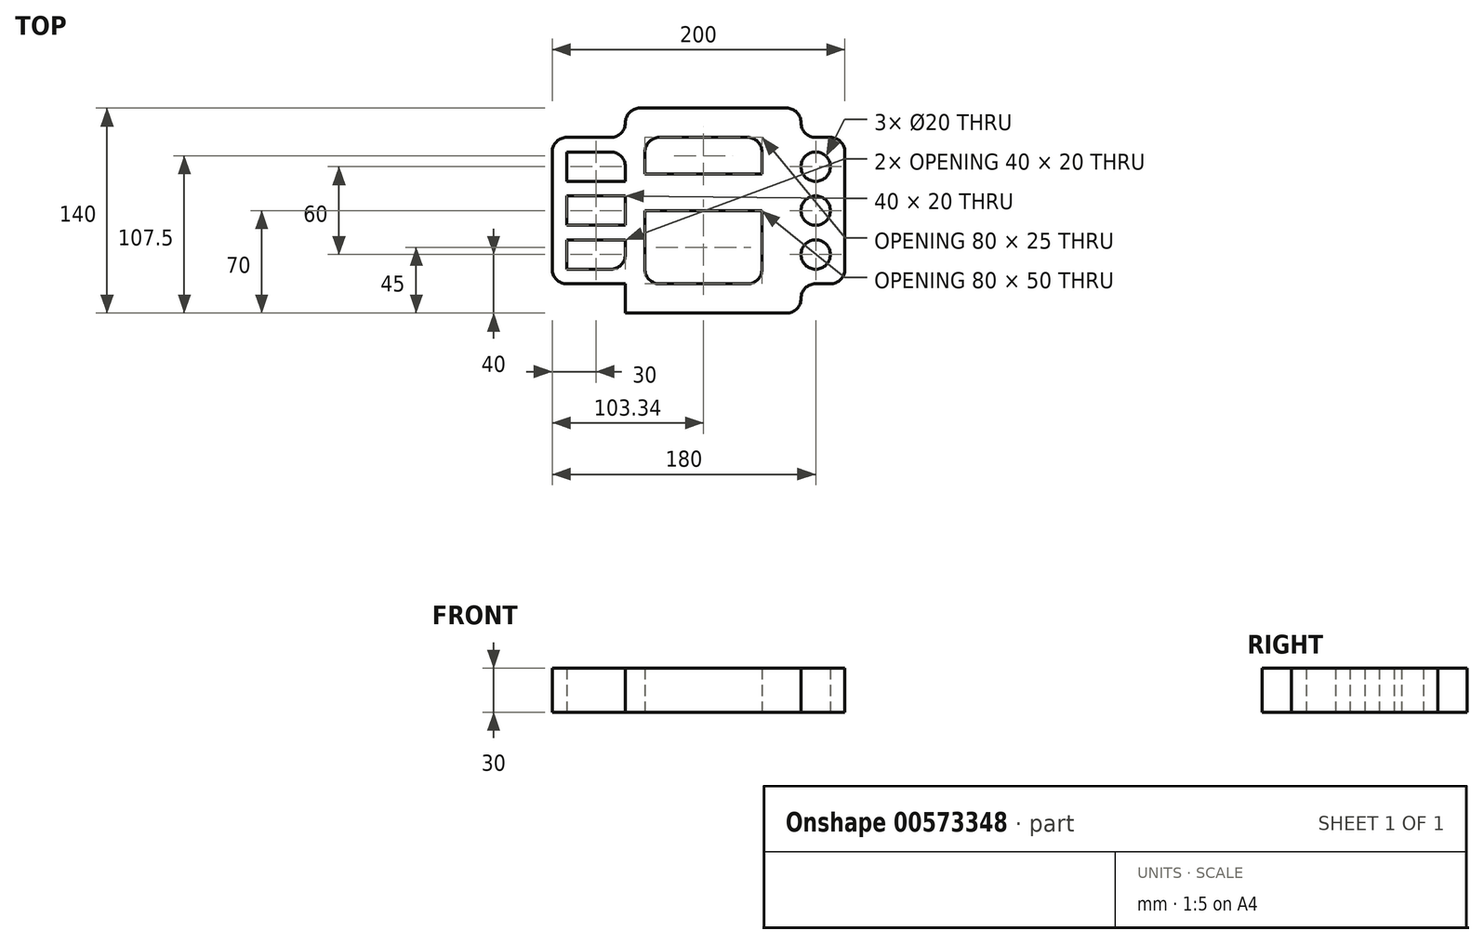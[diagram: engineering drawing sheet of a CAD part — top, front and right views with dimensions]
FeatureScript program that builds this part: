
annotation { "Feature Type Name" : "Feature", "Feature Type Description" : "" }
export const myFeature = defineFeature(function(context is Context, id is Id, definition is map)
    precondition{}
    {
        {
            var Q0;
            Q0=qCreatedBy(makeId("Top.planeOp"),FACE);
            var sketch = newSketch(context, id + "F0", { "sketchPlane" : qUnion([Q0])});
            skLineSegment(sketch, "E0", {"start": v(-50, 30) * mm, "end": v(-50, -50) * mm});
            skLineSegment(sketch, "E1", {"start": v(-40, 40) * mm, "end": v(-13.47, 40) * mm});
            skLineSegment(sketch, "E2", {"start": v(-40, -60) * mm, "end": v(-11.57, -60) * mm});
            skLineSegment(sketch, "E3", {"start": v(0, -70) * mm, "end": v(0, -80) * mm});
            skLineSegment(sketch, "E4", {"start": v(0, 50) * mm, "end": v(0, 50) * mm});
            skPoint(sketch, "E5.orphan", {"position": v(0, 40) * mm});
            skPoint(sketch, "E6.orphan", {"position": v(0, -60) * mm});
            skLineSegment(sketch, "E7", {"start": v(10, 60) * mm, "end": v(110, 60) * mm});
            skLineSegment(sketch, "E8", {"start": v(0, -80) * mm, "end": v(110, -80) * mm});
            skLineSegment(sketch, "E9", {"start": v(120, -70) * mm, "end": v(120, -70) * mm});
            skLineSegment(sketch, "E10", {"start": v(120, 50) * mm, "end": v(120, 50) * mm});
            skLineSegment(sketch, "E11", {"start": v(130, -60) * mm, "end": v(140, -60) * mm});
            skLineSegment(sketch, "E12", {"start": v(130, 40) * mm, "end": v(140, 40) * mm});
            skLineSegment(sketch, "E13", {"start": v(150, 30) * mm, "end": v(150, -50) * mm});
            skPoint(sketch, "E14.trimOffspring.start.orphan", {"position": v(93.34, 40) * mm});
            skCircle(sketch, "E15", {"center": v(130, 20) * mm, "radius": 10 * mm});
            skCircle(sketch, "E16", {"center": v(130, -10) * mm, "radius": 10 * mm});
            skCircle(sketch, "E17", {"center": v(130, -40) * mm, "radius": 10 * mm});
            skLineSegment(sketch, "E18", {"start": v(-40, 30) * mm, "end": v(-40, 10) * mm});
            skLineSegment(sketch, "E19", {"start": v(-40, 30) * mm, "end": v(-10, 30) * mm});
            skLineSegment(sketch, "E20", {"start": v(-40, -50) * mm, "end": v(-10, -50) * mm});
            skLineSegment(sketch, "E21", {"start": v(0, -40) * mm, "end": v(0, -30) * mm});
            skLineSegment(sketch, "E22", {"start": v(-40, 10) * mm, "end": v(0, 10) * mm});
            skLineSegment(sketch, "E23", {"start": v(-40, 0) * mm, "end": v(0, 0) * mm});
            skLineSegment(sketch, "E24", {"start": v(-40, -20) * mm, "end": v(0, -20) * mm});
            skLineSegment(sketch, "E25", {"start": v(-40, -30) * mm, "end": v(0, -30) * mm});
            skLineSegment(sketch, "E26.trimOffspring", {"start": v(0, -20) * mm, "end": v(0, 0) * mm});
            skLineSegment(sketch, "E27.trimOffspring", {"start": v(-40, -30) * mm, "end": v(-40, -50) * mm});
            skLineSegment(sketch, "E28.trimOffspring", {"start": v(-40, 0) * mm, "end": v(-40, -20) * mm});
            skLineSegment(sketch, "E29.trimOffspring", {"start": v(0, 10) * mm, "end": v(0, 20) * mm});
            skPoint(sketch, "E30.visualSharp", {"position": v(0, 30) * mm});
            skArc(sketch, "E30.filletArc", {"start": v(0, 20) * mm, "mid": v(-2.93, 27.07) * mm, "end": v(-10, 30) * mm});
            skPoint(sketch, "E31.visualSharp", {"position": v(0, -50) * mm});
            skArc(sketch, "E31.filletArc", {"start": v(-10, -50) * mm, "mid": v(-2.93, -47.07) * mm, "end": v(0, -40) * mm});
            skPoint(sketch, "E32.trimOffspring.end.orphan", {"position": v(13.34, -60) * mm});
            skPoint(sketch, "E33.start.orphan", {"position": v(81.45, 40) * mm});
            skLineSegment(sketch, "E34", {"start": v(23.34, -60) * mm, "end": v(83.34, -60) * mm});
            skLineSegment(sketch, "E35", {"start": v(93.34, -50) * mm, "end": v(93.34, -10) * mm});
            skLineSegment(sketch, "E36", {"start": v(13.34, -50) * mm, "end": v(13.34, -10) * mm});
            skLineSegment(sketch, "E37", {"start": v(23.34, 40) * mm, "end": v(83.34, 40) * mm});
            skPoint(sketch, "E38.visualSharp", {"position": v(13.34, 40) * mm});
            skArc(sketch, "E38.filletArc", {"start": v(23.34, 40) * mm, "mid": v(16.27, 37.07) * mm, "end": v(13.34, 30) * mm});
            skArc(sketch, "E39.filletArc", {"start": v(93.34, 30) * mm, "mid": v(90.41, 37.07) * mm, "end": v(83.34, 40) * mm});
            skPoint(sketch, "E40.visualSharp", {"position": v(93.34, -60) * mm});
            skArc(sketch, "E40.filletArc", {"start": v(83.34, -60) * mm, "mid": v(90.41, -57.07) * mm, "end": v(93.34, -50) * mm});
            skArc(sketch, "E41.filletArc", {"start": v(13.34, -50) * mm, "mid": v(16.27, -57.07) * mm, "end": v(23.34, -60) * mm});
            skLineSegment(sketch, "E42", {"start": v(-13.47, 40) * mm, "end": v(-10, 40) * mm});
            skArc(sketch, "E43.filletArc", {"start": v(-10, 40) * mm, "mid": v(-2.93, 42.93) * mm, "end": v(0, 50) * mm});
            skPoint(sketch, "E44.visualSharp", {"position": v(0, 60) * mm});
            skArc(sketch, "E44.filletArc", {"start": v(10, 60) * mm, "mid": v(2.93, 57.07) * mm, "end": v(0, 50) * mm});
            skPoint(sketch, "E45.visualSharp", {"position": v(120, 60) * mm});
            skArc(sketch, "E45.filletArc", {"start": v(120, 50) * mm, "mid": v(117.07, 57.07) * mm, "end": v(110, 60) * mm});
            skPoint(sketch, "E46.visualSharp", {"position": v(120, 40) * mm});
            skArc(sketch, "E46.filletArc", {"start": v(120, 50) * mm, "mid": v(122.93, 42.93) * mm, "end": v(130, 40) * mm});
            skLineSegment(sketch, "E47", {"start": v(-11.57, -60) * mm, "end": v(0, -60) * mm});
            skLineSegment(sketch, "E48", {"start": v(0, -70) * mm, "end": v(0, -60) * mm});
            skPoint(sketch, "E49.visualSharp", {"position": v(-50, -60) * mm});
            skArc(sketch, "E49.filletArc", {"start": v(-50, -50) * mm, "mid": v(-47.07, -57.07) * mm, "end": v(-40, -60) * mm});
            skPoint(sketch, "E50.visualSharp", {"position": v(-50, 40) * mm});
            skArc(sketch, "E50.filletArc", {"start": v(-40, 40) * mm, "mid": v(-47.07, 37.07) * mm, "end": v(-50, 30) * mm});
            skPoint(sketch, "E51.visualSharp", {"position": v(120, -60) * mm});
            skArc(sketch, "E51.filletArc", {"start": v(130, -60) * mm, "mid": v(122.93, -62.93) * mm, "end": v(120, -70) * mm});
            skPoint(sketch, "E52.visualSharp", {"position": v(120, -80) * mm});
            skArc(sketch, "E52.filletArc", {"start": v(110, -80) * mm, "mid": v(117.07, -77.07) * mm, "end": v(120, -70) * mm});
            skPoint(sketch, "E53.visualSharp", {"position": v(150, -60) * mm});
            skArc(sketch, "E53.filletArc", {"start": v(140, -60) * mm, "mid": v(147.07, -57.07) * mm, "end": v(150, -50) * mm});
            skPoint(sketch, "E54.visualSharp", {"position": v(150, 40) * mm});
            skArc(sketch, "E54.filletArc", {"start": v(150, 30) * mm, "mid": v(147.07, 37.07) * mm, "end": v(140, 40) * mm});
            skLineSegment(sketch, "E55", {"start": v(13.34, 15) * mm, "end": v(93.34, 15) * mm});
            skLineSegment(sketch, "E56", {"start": v(13.34, -10) * mm, "end": v(93.34, -10) * mm});
            skLineSegment(sketch, "E57.trimOffspring", {"start": v(13.34, 15) * mm, "end": v(13.34, 30) * mm});
            skLineSegment(sketch, "E58.trimOffspring", {"start": v(93.34, 15) * mm, "end": v(93.34, 30) * mm});
            skSolve(sketch);
        }
        {
            var Q0;
            Q0=makeQuery(id+"F0.imprint","IMPRINT",FACE,{"disambiguationData":[TD([[makeQuery(id+"F0.imprint","IMPRINT",EDGE,{"derivedFrom":sQuery(id+"F0.wireOp",EDGE,"E0")}),1.0]])]});
            extrude(context, id + "F1", {"entities" : qUnion([Q0]), "depth" : 30 * mm, "offsetDistance" : 25 * mm});
        }
    });
